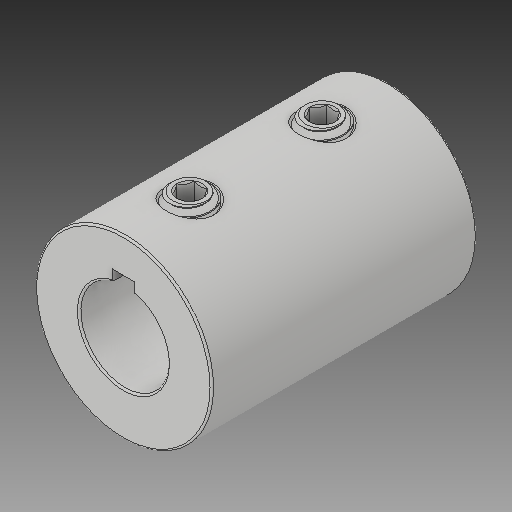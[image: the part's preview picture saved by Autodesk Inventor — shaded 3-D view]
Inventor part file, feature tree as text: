
AUTODESK INVENTOR PART (.ipt)
format: ipt  version: 2019 (Build 230136000, 136)  size: 578,560 bytes
history: native  units: in
note: dims shown in document units (in); Inventor stores cm internally (conversion verified against a paired STEP export)
features: other x2, fillet x1
ambient origin geometry x8: Origin, YZ Plane, XZ Plane, XY Plane, X Axis, Y Axis, Z Axis, Center Point
bodies: Solid1 (feature_tree), Solid2 (feature_tree), Solid3 (feature_tree)
feature tree (3):
  other  "Cut-Extrude3"
  other  "LPattern1"
  fillet  "Fillet1"  [1 undecoded]
note: 1 required parameter value undecoded (feature->parameter linkage not recoverable at this tier; creation-order binding heuristic only, values carry confidence <= 0.55)
